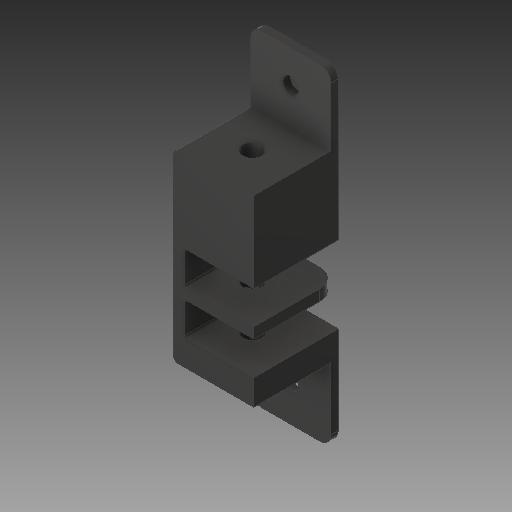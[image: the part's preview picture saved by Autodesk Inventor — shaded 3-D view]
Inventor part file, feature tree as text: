
AUTODESK INVENTOR PART (.ipt)
format: ipt  version: 2019 (Build 230136000, 136)  size: 201,728 bytes
history: native  units: mm
features: extrude x5, sketch x5, fillet x3, mirror x2, thicken_offset x1
ambient origin geometry x8: Origin, YZ Plane, XZ Plane, XY Plane, X Axis, Y Axis, Z Axis, Center Point
bodies: Body1 (feature_tree)
feature tree (16):
  extrude  "Extrusion3"  Depth=3.0mm
  extrude  "Extrusion11"  Depth=23.0mm TaperAngle=0.0deg
  mirror  "Mirror1"
  extrude  "Extrusion13"  Depth=2.0mm TaperAngle=0.0deg
  extrude  "Extrusion14"  Depth=9.0mm
  extrude  "Extrusion15"  Depth=1.0mm
  mirror  "Mirror2"
  fillet  "Fillet2"  Radius=10.0mm
  fillet  "Fillet3"  Radius=5.2mm
  fillet  "Fillet4"  Radius=10.0mm
  thicken_offset  "Thicken1"
  sketch  "Sketch3"  dims[d7=50.0mm d8=3.0mm]
  sketch  "Sketch11"  dims[d9=3.0mm d10=23.0mm d11=0.0mm]
  sketch  "Sketch13"  dims[d46=20.0mm d47=2.0mm d48=0.0mm]
  sketch  "Sketch14"  dims[d58=3.0mm d62=9.0mm]
  sketch  "Sketch15"  dims[d63=9.0mm d64=4.0mm d65=10.0mm d66=0.0mm d67=5.2mm d68=10.0mm d69=0.0mm d70=4.4mm d71=10.0mm d72=10.0mm d73=0.0mm d74=5.0mm d75=3.0mm d76=0.5mm d77=1.0mm d78=1.0mm d79=1.0mm]
